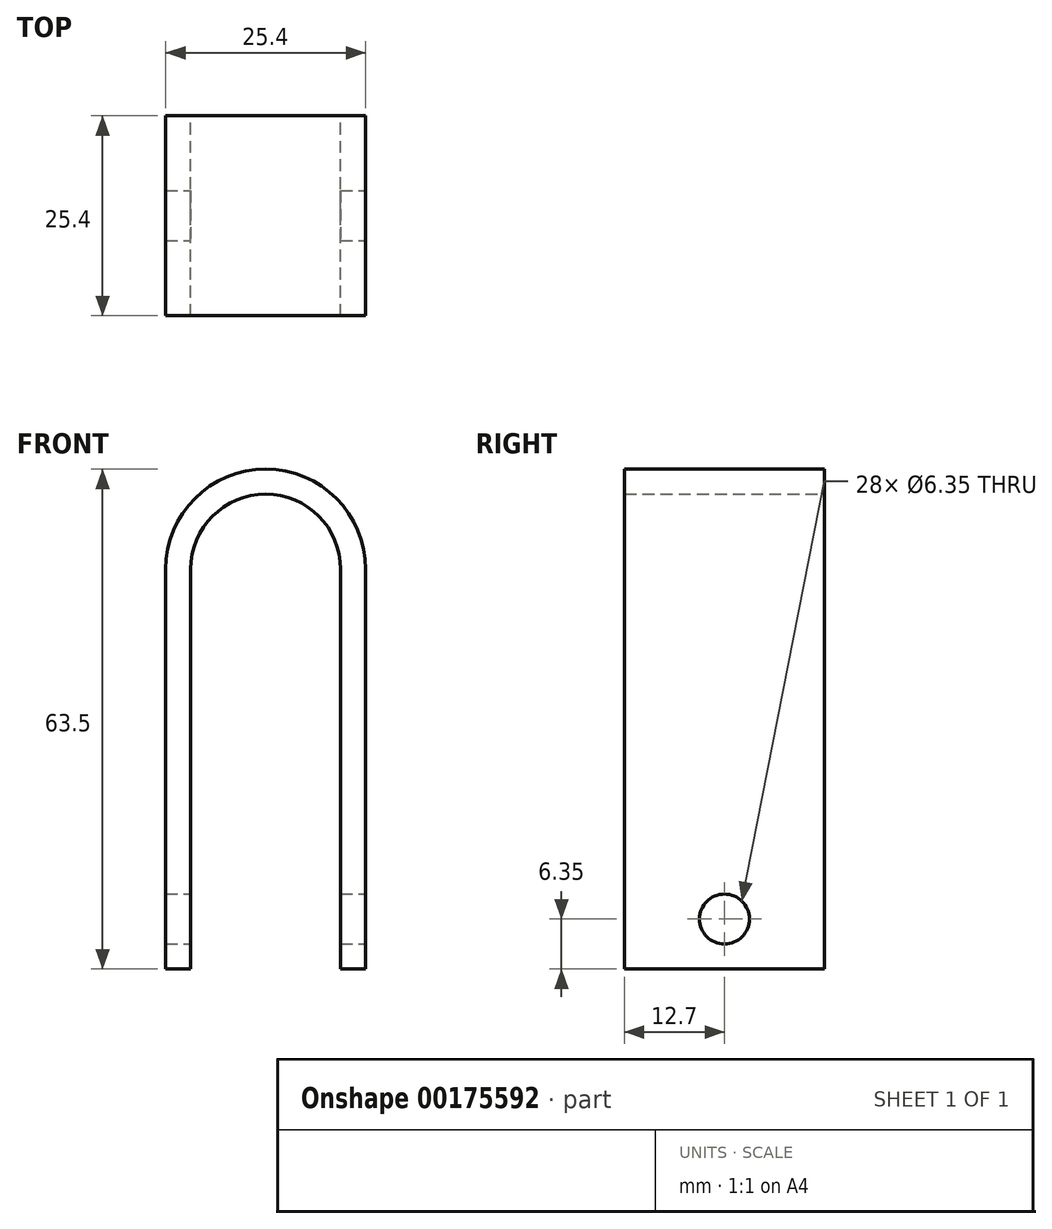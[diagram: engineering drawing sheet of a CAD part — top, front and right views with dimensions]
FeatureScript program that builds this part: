
annotation { "Feature Type Name" : "Feature", "Feature Type Description" : "" }
export const myFeature = defineFeature(function(context is Context, id is Id, definition is map)
    precondition{}
    {
        {
            var Q0;
            Q0=qCreatedBy(makeId("Front.planeOp"),FACE);
            var sketch = newSketch(context, id + "F0", { "sketchPlane" : qUnion([Q0])});
            skLineSegment(sketch, "E0.left", {"start": v(-12.7, 25.4) * mm, "end": v(-12.7, -25.4) * mm});
            skLineSegment(sketch, "E0.right", {"start": v(12.7, 25.4) * mm, "end": v(12.7, -25.4) * mm});
            skPoint(sketch, "E0.middle", {"position": v(0, 0) * mm});
            skArc(sketch, "E1", {"start": v(12.7, 25.4) * mm, "mid": v(0, 38.1) * mm, "end": v(-12.7, 25.4) * mm});
            skArc(sketch, "E2.0", {"start": v(9.53, 25.4) * mm, "mid": v(0, 34.93) * mm, "end": v(-9.52, 25.4) * mm});
            skLineSegment(sketch, "E3", {"start": v(-9.52, 25.4) * mm, "end": v(-9.52, -25.4) * mm});
            skLineSegment(sketch, "E4", {"start": v(9.53, 25.4) * mm, "end": v(9.53, -25.4) * mm});
            skLineSegment(sketch, "E5", {"start": v(-12.7, -25.4) * mm, "end": v(-9.52, -25.4) * mm});
            skLineSegment(sketch, "E6", {"start": v(9.53, -25.4) * mm, "end": v(12.7, -25.4) * mm});
            skSolve(sketch);
        }
        {
            var Q0;
            Q0=makeQuery(id+"F0.imprint","IMPRINT",FACE,{"disambiguationData":[TD([[makeQuery(id+"F0.imprint","IMPRINT",EDGE,{"derivedFrom":sQuery(id+"F0.wireOp",EDGE,"E0.left")}),1.0]])]});
            extrude(context, id + "F1", {"entities" : qUnion([Q0]), "depth" : 25.4 * mm});
        }
        {
            var Q0;
            Q0=makeQuery(id+"F1.opExtrude","SWEPT_FACE",FACE,{"disambiguationData":[OSD([sQuery(id+"F0.wireOp",EDGE,"E0.left")])]});
            var sketch = newSketch(context, id + "F2", { "sketchPlane" : qUnion([Q0])});
            skLineSegment(sketch, "E7", {"start": v(12.7, -25.4) * mm, "end": v(12.7, -19.05) * mm});
            skCircle(sketch, "E8", {"center": v(12.7, -19.05) * mm, "radius": 3.18 * mm});
            skSolve(sketch);
        }
        {
            var Q0;
            Q0=makeQuery(id+"F2.imprint","IMPRINT",FACE,{"disambiguationData":[TD([[makeQuery(id+"F2.imprint","IMPRINT",EDGE,{"derivedFrom":sQuery(id+"F2.wireOp",EDGE,"E8")}),1.0]])]});
            extrude(context, id + "F3", {"entities" : qUnion([Q0]), "operationType" : NewBodyOperationType.REMOVE, "endBound" : BoundingType.SYMMETRIC, "depth" : 101.6 * mm});
        }
    });
